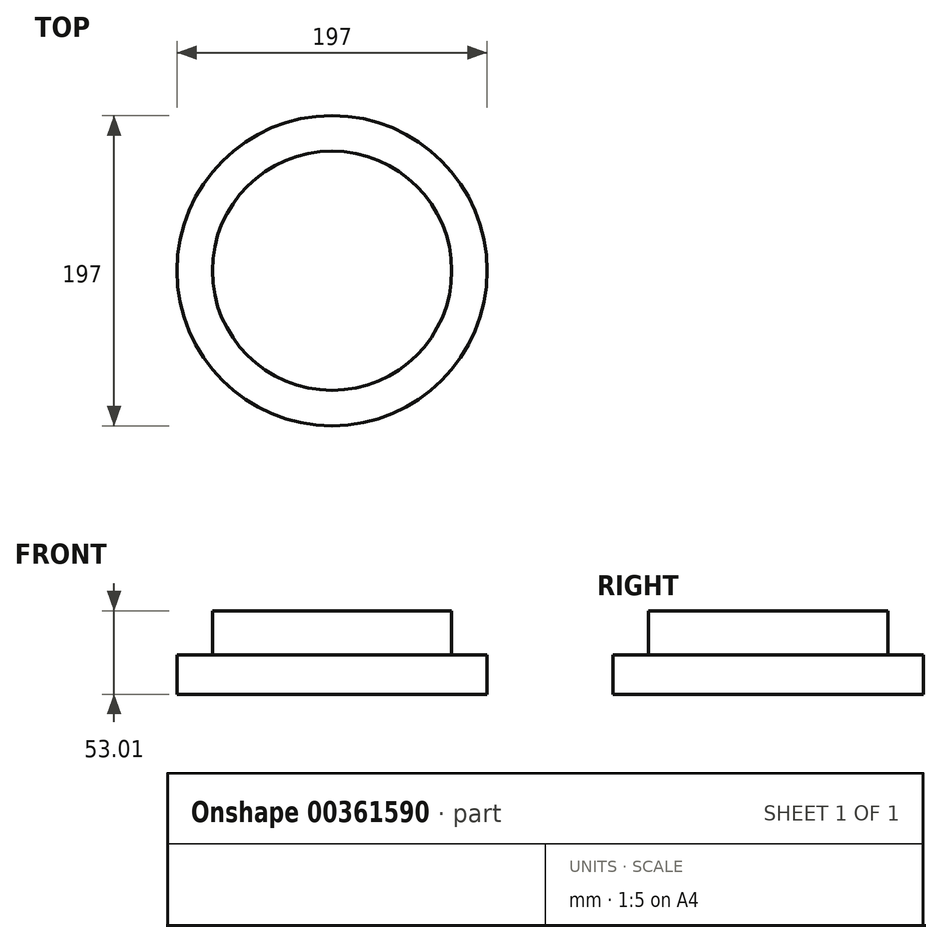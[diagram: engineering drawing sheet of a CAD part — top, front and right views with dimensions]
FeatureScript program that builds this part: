
annotation { "Feature Type Name" : "Feature", "Feature Type Description" : "" }
export const myFeature = defineFeature(function(context is Context, id is Id, definition is map)
    precondition{}
    {
        {
            var Q0;
            Q0=qCreatedBy(makeId("Top.planeOp"),FACE);
            var sketch = newSketch(context, id + "F0", { "sketchPlane" : qUnion([Q0])});
            skCircle(sketch, "E0", {"center": v(0, 0) * mm, "radius": 98.5 * mm});
            skCircle(sketch, "E1", {"center": v(0, 0) * mm, "radius": 76 * mm});
            skPoint(sketch, "E2.visualSharp", {"position": v(-50.04, 52.39) * mm});
            skPoint(sketch, "E3.visualSharp", {"position": v(50.04, 52.39) * mm});
            skPoint(sketch, "E4.visualSharp", {"position": v(50.04, -52.39) * mm});
            skPoint(sketch, "E5.visualSharp", {"position": v(-50.04, -52.39) * mm});
            skSolve(sketch);
        }
        {
            var Q0;
            Q0=makeQuery(id+"F0.imprint","IMPRINT",FACE,{"disambiguationData":[TD([[makeQuery(id+"F0.imprint","IMPRINT",EDGE,{"derivedFrom":sQuery(id+"F0.wireOp",EDGE,"E0")}),1.0]])]});
            extrude(context, id + "F1", {"entities" : qUnion([Q0]), "depth" : 25 * mm});
        }
        {
            var Q0;
            Q0=makeQuery(id+"F0.imprint","IMPRINT",FACE,{"disambiguationData":[TD([[makeQuery(id+"F0.imprint","IMPRINT",EDGE,{"derivedFrom":sQuery(id+"F0.wireOp",EDGE,"E1")}),1.0]])]});
            var Q1;
            Q1=makeQuery(id+"F0.imprint","IMPRINT",FACE,{"disambiguationData":[TD([[makeQuery(id+"F0.imprint","IMPRINT",EDGE,{"derivedFrom":sQuery(id+"F0.wireOp",EDGE,"C2Vx0xNm-KQQi-DTvS-tQ2f-jN9590WCwXLG")}),1.0]])]});
            extrude(context, id + "F2", {"entities" : qUnion([Q0, Q1]), "operationType" : NewBodyOperationType.ADD, "depth" : 53 * mm, "hasDraft" : true, "draftAngle" : 0 * degree});
        }
        {
            var Q0;
            Q0=sQuery(id+"F0.wireOp",EDGE,"E0");
            var Q1;
            Q1=sQuery(id+"F0.wireOp",EDGE,"E1");
            var Q2;
            Q2=sQuery(id+"F0.wireOp",EDGE,"2U8aNyld-8Bkl-hgVt-TkNV-Q5sWzwI6qBuH.bottom");
            var Q3;
            Q3=sQuery(id+"F0.wireOp",EDGE,"2U8aNyld-8Bkl-hgVt-TkNV-Q5sWzwI6qBuH.left");
            var Q4;
            Q4=sQuery(id+"F0.wireOp",EDGE,"2U8aNyld-8Bkl-hgVt-TkNV-Q5sWzwI6qBuH.right");
            var Q5;
            Q5=sQuery(id+"F0.wireOp",EDGE,"E2.filletArc");
            var Q6;
            Q6=sQuery(id+"F0.wireOp",EDGE,"E3.filletArc");
            var Q7;
            Q7=sQuery(id+"F0.wireOp",EDGE,"E4.filletArc");
            var Q8;
            Q8=sQuery(id+"F0.wireOp",EDGE,"E5.filletArc");
            extrude(context, id + "F3", {"bodyType" : ToolBodyType.SURFACE, "surfaceEntities" : qUnion([Q0, Q1, Q2, Q3, Q4, Q5, Q6, Q7, Q8]), "depth" : 25.4 * mm});
        }
    });
